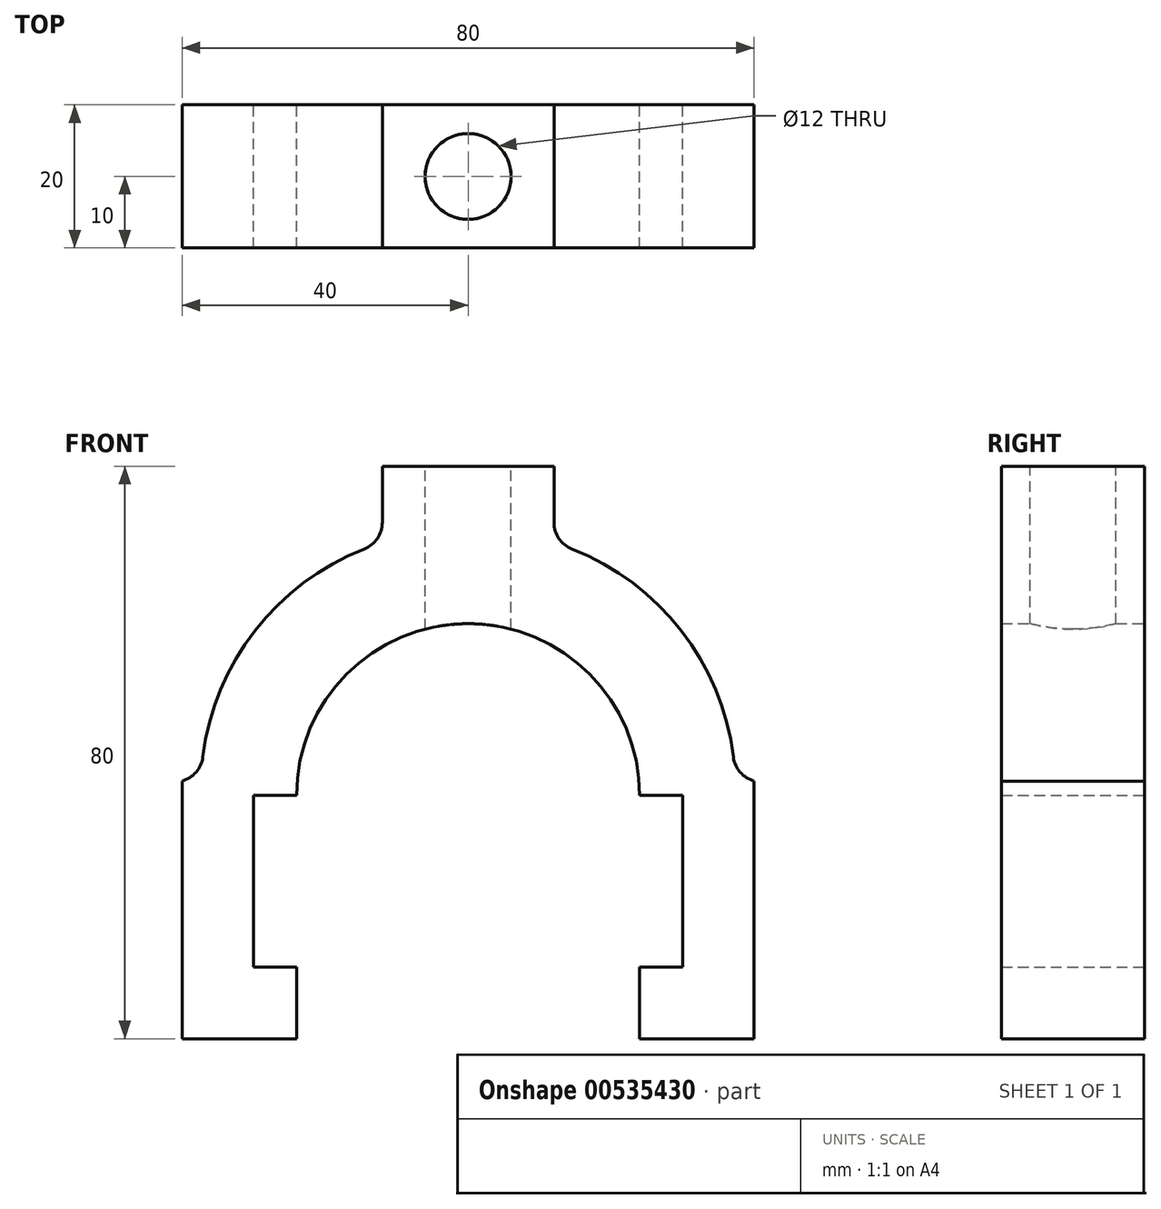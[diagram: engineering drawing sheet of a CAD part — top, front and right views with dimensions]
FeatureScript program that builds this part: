
annotation { "Feature Type Name" : "Feature", "Feature Type Description" : "" }
export const myFeature = defineFeature(function(context is Context, id is Id, definition is map)
    precondition{}
    {
        {
            var Q0;
            Q0=qCreatedBy(makeId("Front.planeOp"),FACE);
            var sketch = newSketch(context, id + "F0", { "sketchPlane" : qUnion([Q0])});
            skLineSegment(sketch, "E0", {"start": v(0, 0) * mm, "end": v(16, 0) * mm});
            skLineSegment(sketch, "E1", {"start": v(16, 0) * mm, "end": v(16, 36) * mm});
            skLineSegment(sketch, "E2", {"start": v(0, 0) * mm, "end": v(0, 10) * mm});
            skLineSegment(sketch, "E3", {"start": v(0, 10) * mm, "end": v(6, 10) * mm});
            skLineSegment(sketch, "E4", {"start": v(6, 10) * mm, "end": v(6, 34) * mm});
            skLineSegment(sketch, "E5", {"start": v(6, 34) * mm, "end": v(0, 34) * mm});
            skLineSegment(sketch, "E6", {"start": v(0, 34) * mm, "end": v(-24, 34) * mm, "construction": true});
            skArc(sketch, "E7", {"start": v(0, 34) * mm, "mid": v(-7.03, 50.97) * mm, "end": v(-24, 58) * mm});
            skLineSegment(sketch, "E8", {"start": v(-24, 0) * mm, "end": v(-24, 80) * mm, "construction": true});
            skLineSegment(sketch, "E9.trimOffspring", {"start": v(-12, 72.16) * mm, "end": v(-12, 80) * mm});
            skArc(sketch, "E10.trimOffspring", {"start": v(13.1, 39.36) * mm, "mid": v(5.8, 57) * mm, "end": v(-9.46, 68.43) * mm});
            skPoint(sketch, "E11.visualSharp", {"position": v(-12, 69.32) * mm});
            skArc(sketch, "E11.filletArc", {"start": v(-12, 72.16) * mm, "mid": v(-11.3, 69.9) * mm, "end": v(-9.46, 68.43) * mm});
            skPoint(sketch, "E12.visualSharp", {"position": v(13.35, 36) * mm});
            skArc(sketch, "E12.filletArc", {"start": v(13.1, 39.36) * mm, "mid": v(14.04, 37.24) * mm, "end": v(16, 36) * mm});
            skLineSegment(sketch, "E13", {"start": v(-24, 80) * mm, "end": v(-12, 80) * mm});
            skLineSegment(sketch, "E14.MirrorCS", {"start": v(-64, 36) * mm, "end": v(-64, 36) * mm});
            skArc(sketch, "E15.MirrorCS", {"start": v(-36, 72.16) * mm, "mid": v(-36.7, 69.9) * mm, "end": v(-38.54, 68.43) * mm});
            skArc(sketch, "E16.MirrorCS", {"start": v(-61.1, 39.36) * mm, "mid": v(-62.04, 37.24) * mm, "end": v(-64, 36) * mm});
            skPoint(sketch, "E17.MirrorP", {"position": v(-36, 69.32) * mm});
            skLineSegment(sketch, "E18.MirrorCS", {"start": v(-48, 34) * mm, "end": v(-24, 34) * mm, "construction": true});
            skArc(sketch, "E19.MirrorCS", {"start": v(-48, 34) * mm, "mid": v(-40.97, 50.97) * mm, "end": v(-24, 58) * mm});
            skLineSegment(sketch, "E20.MirrorCS", {"start": v(-36, 72.16) * mm, "end": v(-36, 80) * mm});
            skArc(sketch, "E21.MirrorCS", {"start": v(-61.1, 39.36) * mm, "mid": v(-53.8, 57) * mm, "end": v(-38.54, 68.43) * mm});
            skLineSegment(sketch, "E22.MirrorCS", {"start": v(-24, 80) * mm, "end": v(-36, 80) * mm});
            skLineSegment(sketch, "E23.MirrorCS", {"start": v(-64, 0) * mm, "end": v(-64, 36) * mm});
            skLineSegment(sketch, "E24.MirrorCS", {"start": v(-48, 10) * mm, "end": v(-54, 10) * mm});
            skPoint(sketch, "E25.MirrorP", {"position": v(-61.35, 36) * mm});
            skLineSegment(sketch, "E26.MirrorCS", {"start": v(-48, 0) * mm, "end": v(-48, 10) * mm});
            skLineSegment(sketch, "E27.MirrorCS", {"start": v(-48, 0) * mm, "end": v(-64, 0) * mm});
            skLineSegment(sketch, "E28.MirrorCS", {"start": v(-54, 10) * mm, "end": v(-54, 34) * mm});
            skLineSegment(sketch, "E29.MirrorCS", {"start": v(-54, 34) * mm, "end": v(-48, 34) * mm});
            skSolve(sketch);
        }
        {
            var Q0;
            Q0 = qSketchRegion(id + "F0", true);
            extrude(context, id + "F1", {"entities" : qUnion([Q0]), "depth" : 20 * mm, "offsetDistance" : 25 * mm});
        }
        {
            var Q0;
            Q0=makeQuery(id+"F1.opExtrude","SWEPT_FACE",FACE,{"disambiguationData":[OSD([sQuery(id+"F0.wireOp",EDGE,"E13"),sQuery(id+"F0.wireOp",EDGE,"E22.MirrorCS")])]});
            var sketch = newSketch(context, id + "F2", { "sketchPlane" : qUnion([Q0])});
            skCircle(sketch, "E30", {"center": v(-24, -10) * mm, "radius": 6 * mm});
            skSolve(sketch);
        }
        {
            var Q0;
            Q0 = qSketchRegion(id + "F2", true);
            extrude(context, id + "F3", {"entities" : qUnion([Q0]), "operationType" : NewBodyOperationType.REMOVE, "endBound" : BoundingType.THROUGH_ALL, "oppositeDirection" : true, "depth" : 25 * mm, "offsetDistance" : 25 * mm});
        }
    });
